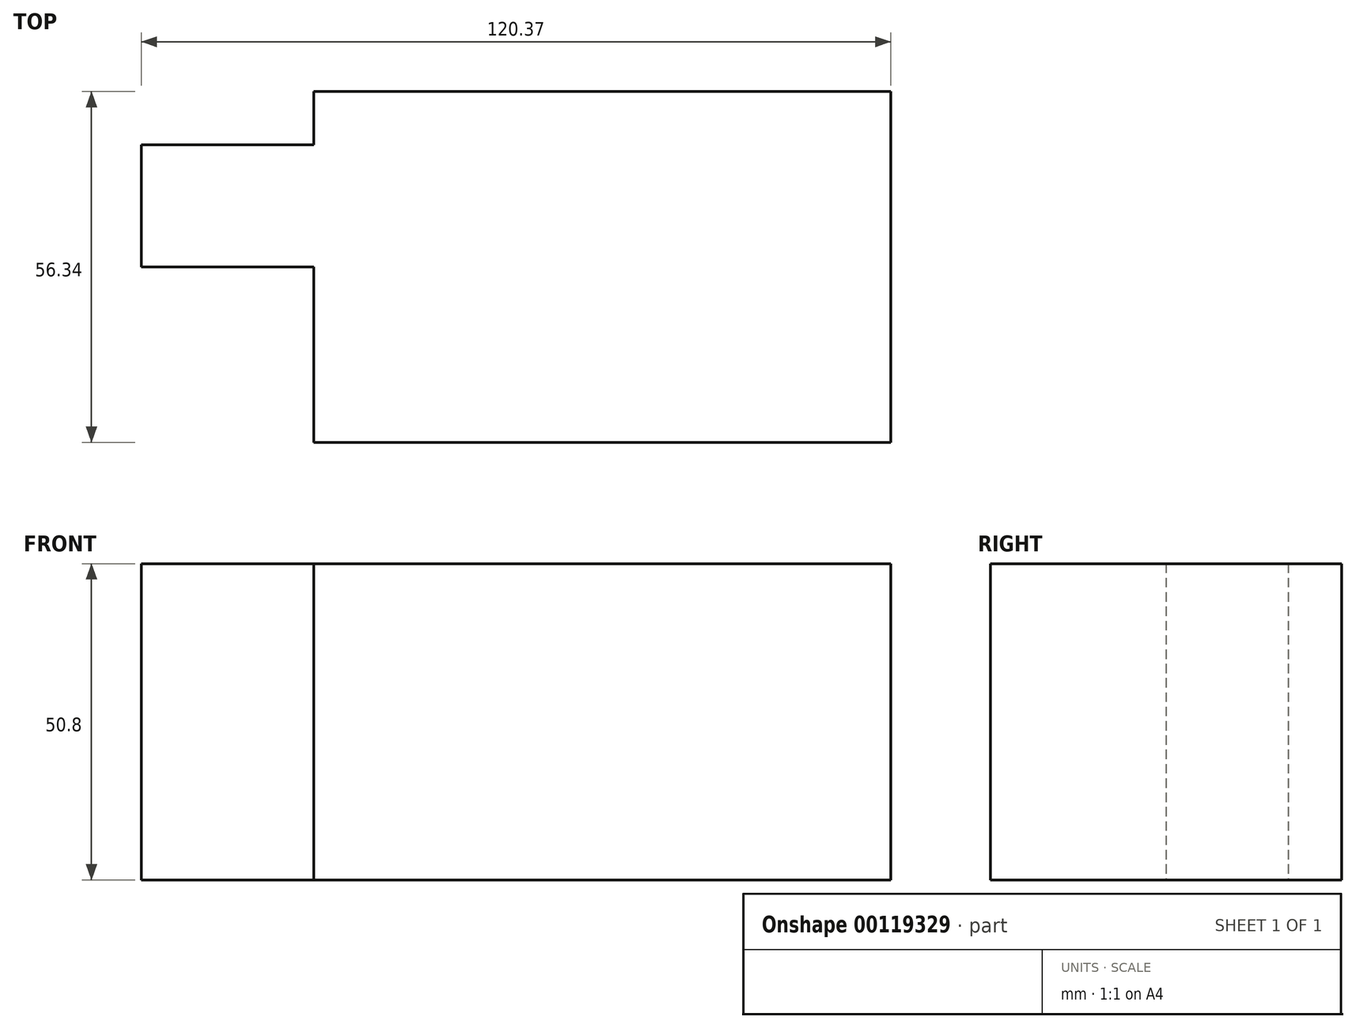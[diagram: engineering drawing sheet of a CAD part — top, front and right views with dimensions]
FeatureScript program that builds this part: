
annotation { "Feature Type Name" : "Feature", "Feature Type Description" : "" }
export const myFeature = defineFeature(function(context is Context, id is Id, definition is map)
    precondition{}
    {
        {
            var Q0;
            Q0=qCreatedBy(makeId("Top.planeOp"),FACE);
            var sketch = newSketch(context, id + "F0", { "sketchPlane" : qUnion([Q0])});
            skLineSegment(sketch, "E0.bottom", {"start": v(-41.36, 0) * mm, "end": v(51.34, 0) * mm});
            skLineSegment(sketch, "E0.top", {"start": v(-41.36, 56.34) * mm, "end": v(51.34, 56.34) * mm});
            skLineSegment(sketch, "E0.left", {"start": v(-41.36, 0) * mm, "end": v(-41.36, 56.34) * mm});
            skLineSegment(sketch, "E0.right", {"start": v(51.34, 0) * mm, "end": v(51.34, 56.34) * mm});
            skLineSegment(sketch, "E1.bottom", {"start": v(-41.36, 28.17) * mm, "end": v(-69.03, 28.17) * mm});
            skLineSegment(sketch, "E1.top", {"start": v(-41.36, 47.78) * mm, "end": v(-69.03, 47.78) * mm});
            skLineSegment(sketch, "E1.left", {"start": v(-41.36, 28.17) * mm, "end": v(-41.36, 47.78) * mm});
            skLineSegment(sketch, "E1.right", {"start": v(-69.03, 28.17) * mm, "end": v(-69.03, 47.78) * mm});
            skSolve(sketch);
        }
        {
            var Q0;
            Q0=makeQuery(id+"F0.imprint","IMPRINT",FACE,{"disambiguationData":[TD([[makeQuery(id+"F0.imprint","IMPRINT",EDGE,{"derivedFrom":sQuery(id+"F0.wireOp",EDGE,"E1.bottom")}),-1.0]])]});
            var Q1;
            {var subQ4=sQuery(id+"F0.wireOp",EDGE,"E0.top");Q1=makeQuery(id+"F0.imprint","IMPRINT",FACE,{"disambiguationData":[TD([[makeQuery(id+"F0.imprint","IMPRINT",EDGE,{"derivedFrom":subQ4}),-1.0]])]});}
            extrude(context, id + "F1", {"entities" : qUnion([Q0, Q1]), "depth" : 50.8 * mm});
        }
    });
